# Revit family: P190780JX-158c_JXL6536HSS_StainlessSteel_JA_Cooking_Ventilation
name_source: partatom
category: Specialty Equipment
units: mm (PartAtom-declared; Revit-internal decimal feet)

## family parameters
Always vertical = Yes
Cut with Voids When Loaded = No
Maintain Annotation Orientation = No
Part Type = Normal
Room Calculation Point = No
Round Connector Dimension = Use Diameter
Shared = No
Work Plane-Based = No

## types (1)
- JXL6536HSS
    Accent Material = ARCAT - Metal - Steel - Gray
    Amps = 15 A
    Body Material = ARCAT - Metal - Steel - Stainless
    Default Elevation = 0"
    Depth = 22"
    Description = Stainless Steel 36" Custom Hood Liner
Revêtement de hotte personnalisé, 36 po
    Family Name = COMMERCIAL & LINER HOODS - 36"
    Feature 1 = Optional 600 CFM or 1,200 CFM Internal Blower
Ventilateur interne facultatif de 600 ou 1200 pi³/min
    Feature 2 = Optional 1,200 CFM In-Line Blower
Ventilateur en ligne facultatif de 1200 pi³/min
    Feature 3 = 10-Inch Round Exterior Venting
Ventilation extérieure ronde de 10 po
    Height = 11 1/2"
    Installation-Fabrication = http://access.whirlpool.com Instruction&sku=JXL6536HSS&language=EN
http://access.whirlpool.com Instruction&sku=JXL6536HSS&language=EN
    Knob Material = ARCAT - Metal - Steel - Black
    Manufacturer = Jenn Air
    Model = JXL6536HSS
    Vent Material = ARCAT - Metal - Steel - Gray
    Voltage = 0 V
    Width = 35 7/8"

## geometry (parser evidence)
native form markers: Sweep x4
no freeform markers — native parametric forms only
